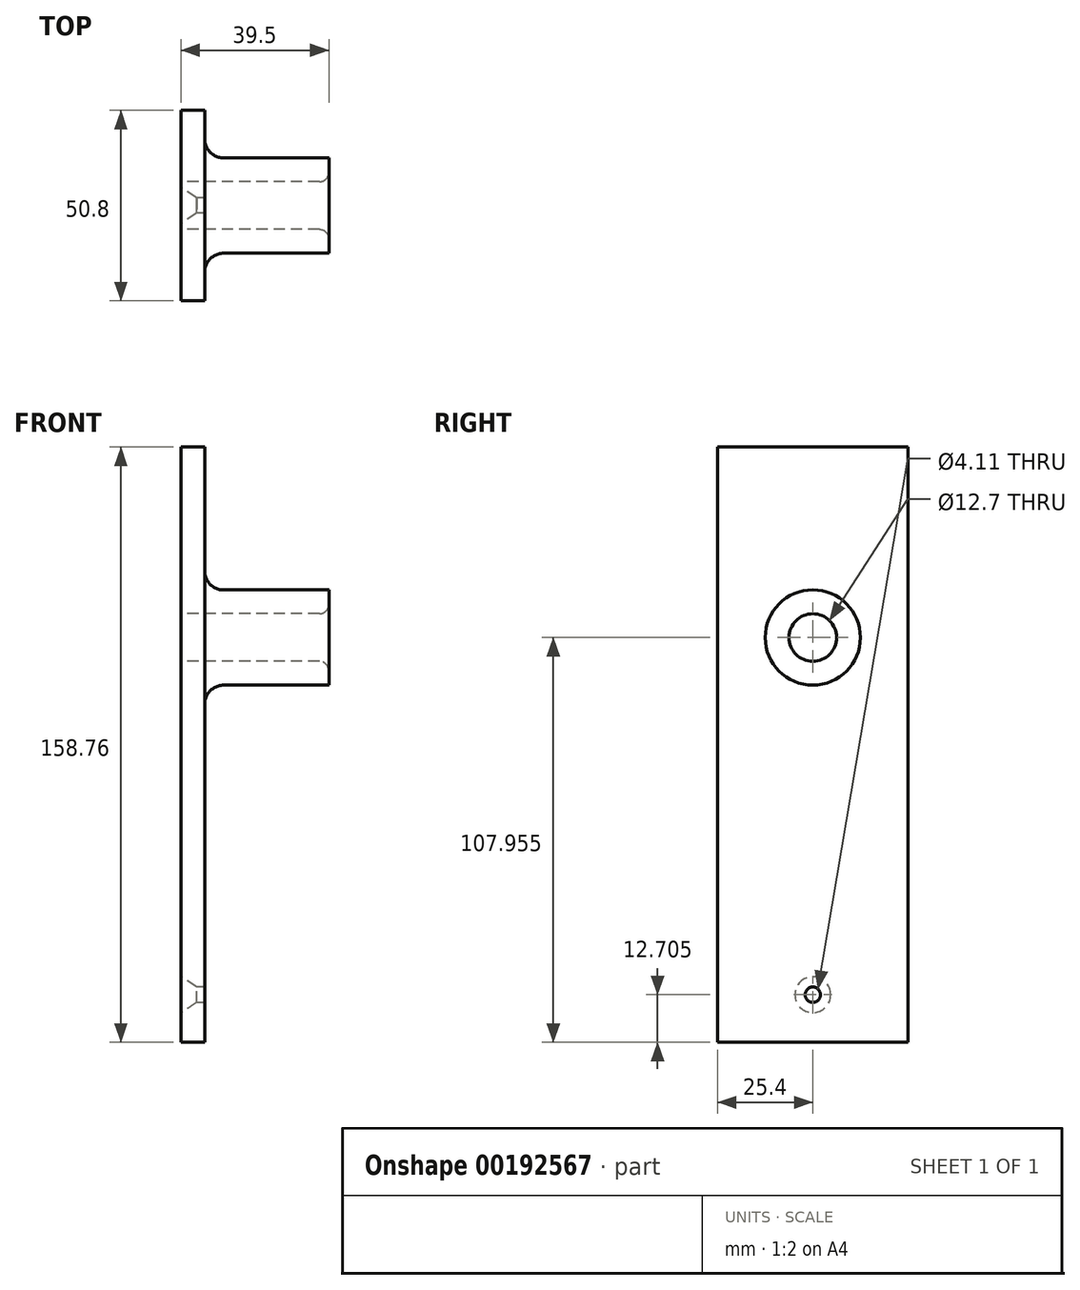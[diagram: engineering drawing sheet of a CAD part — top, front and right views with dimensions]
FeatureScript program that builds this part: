
annotation { "Feature Type Name" : "Feature", "Feature Type Description" : "" }
export const myFeature = defineFeature(function(context is Context, id is Id, definition is map)
    precondition{}
    {
        {
            var Q0;
            Q0=qCreatedBy(makeId("Right.planeOp"),FACE);
            var sketch = newSketch(context, id + "F0", { "sketchPlane" : qUnion([Q0])});
            skLineSegment(sketch, "E0.bottom", {"start": v(-25.4, 79.38) * mm, "end": v(25.4, 79.38) * mm});
            skLineSegment(sketch, "E0.top", {"start": v(-25.4, -79.37) * mm, "end": v(25.4, -79.37) * mm});
            skLineSegment(sketch, "E0.left", {"start": v(-25.4, 79.38) * mm, "end": v(-25.4, -79.37) * mm});
            skLineSegment(sketch, "E0.right", {"start": v(25.4, 79.38) * mm, "end": v(25.4, -79.37) * mm});
            skPoint(sketch, "E0.middle", {"position": v(0, 0) * mm});
            skLineSegment(sketch, "E1", {"start": v(0, 79.38) * mm, "end": v(0, 28.57) * mm});
            skPoint(sketch, "E1.endSnap0", {"position": v(0, 79.38) * mm});
            skLineSegment(sketch, "E2", {"start": v(0, 28.57) * mm, "end": v(0, -41.28) * mm});
            skLineSegment(sketch, "E3", {"start": v(0, -41.28) * mm, "end": v(0, -53.98) * mm});
            skLineSegment(sketch, "E4", {"start": v(0, -53.98) * mm, "end": v(0, -79.37) * mm});
            skCircle(sketch, "E5", {"center": v(0, 28.57) * mm, "radius": 12.7 * mm});
            skCircle(sketch, "E6", {"center": v(0, 28.57) * mm, "radius": 6.35 * mm});
            skCircle(sketch, "E7", {"center": v(0, -66.67) * mm, "radius": 2.06 * mm});
            skSolve(sketch);
        }
        {
            var Q0;
            {var subQ1=sQuery(id+"F0.wireOp",EDGE,"E0.left");Q0=makeQuery(id+"F0.imprint","IMPRINT",FACE,{"disambiguationData":[TD([[makeQuery(id+"F0.imprint","IMPRINT",EDGE,{"derivedFrom":subQ1}),1.0]])]});}
            var Q1;
            {var subQ1=sQuery(id+"F0.wireOp",EDGE,"E0.right");Q1=makeQuery(id+"F0.imprint","IMPRINT",FACE,{"disambiguationData":[TD([[makeQuery(id+"F0.imprint","IMPRINT",EDGE,{"derivedFrom":subQ1}),-1.0]])]});}
            var Q2;
            {var subQ0=sQuery(id+"F0.wireOp",EDGE,"E5");var subQ1=sQuery(id+"F0.wireOp",EDGE,"E1");var subQ2=makeQuery(id+"F0.imprint","INTERSECT",VERTEX,{"derivedFrom":[subQ1,subQ0]});Q2=makeQuery(id+"F0.imprint","IMPRINT",FACE,{"disambiguationData":[TD([[makeQuery(id+"F0.imprint","IMPRINT",EDGE,{"disambiguationData":[TD([[subQ2,-1.0]])],"derivedFrom":subQ1}),-1.0]])]});}
            var Q3;
            {var subQ0=sQuery(id+"F0.wireOp",EDGE,"E5");var subQ1=sQuery(id+"F0.wireOp",EDGE,"E1");var subQ2=makeQuery(id+"F0.imprint","INTERSECT",VERTEX,{"derivedFrom":[subQ1,subQ0]});Q3=makeQuery(id+"F0.imprint","IMPRINT",FACE,{"disambiguationData":[TD([[makeQuery(id+"F0.imprint","IMPRINT",EDGE,{"disambiguationData":[TD([[subQ2,-1.0]])],"derivedFrom":subQ1}),1.0]])]});}
            extrude(context, id + "F1", {"entities" : qUnion([Q0, Q1, Q2, Q3]), "depth" : 6.35 * mm});
        }
        {
            var Q0;
            {var subQ0=sQuery(id+"F0.wireOp",EDGE,"E5");var subQ1=sQuery(id+"F0.wireOp",EDGE,"E1");var subQ2=makeQuery(id+"F0.imprint","INTERSECT",VERTEX,{"derivedFrom":[subQ1,subQ0]});Q0=makeQuery(id+"F0.imprint","IMPRINT",FACE,{"disambiguationData":[TD([[makeQuery(id+"F0.imprint","IMPRINT",EDGE,{"disambiguationData":[TD([[subQ2,-1.0]])],"derivedFrom":subQ1}),-1.0]])]});}
            var Q1;
            {var subQ0=sQuery(id+"F0.wireOp",EDGE,"E5");var subQ1=sQuery(id+"F0.wireOp",EDGE,"E1");var subQ2=makeQuery(id+"F0.imprint","INTERSECT",VERTEX,{"derivedFrom":[subQ1,subQ0]});Q1=makeQuery(id+"F0.imprint","IMPRINT",FACE,{"disambiguationData":[TD([[makeQuery(id+"F0.imprint","IMPRINT",EDGE,{"disambiguationData":[TD([[subQ2,-1.0]])],"derivedFrom":subQ1}),1.0]])]});}
            extrude(context, id + "F2", {"entities" : qUnion([Q0, Q1]), "operationType" : NewBodyOperationType.ADD, "depth" : 39.5 * mm});
        }
        {
            var Q0;
            Q0=makeQuery(id+"F1.opExtrude","CAP_EDGE",EDGE,{"disambiguationData":[OSD([sQuery(id+"F0.wireOp",EDGE,"E7")])],"isStart":true});
            chamfer(context, id + "F3", {"entities" : qUnion([Q0]), "chamferType" : ChamferType.TWO_OFFSETS, "width1" : 2.72 * mm, "oppositeDirection" : false, "width2" : 4.27 * mm, "tangentPropagation" : true});
        }
        {
            var Q0;
            Q0=makeQuery(id+"F2.boolean.opBoolean","INTERSECT",EDGE,{"derivedFrom":[makeQuery(id+"F1.opExtrude","CAP_FACE",FACE,{"disambiguationData":[OSD([sQuery(id+"F0.wireOp",EDGE,"E0.bottom"),sQuery(id+"F0.wireOp",EDGE,"E0.top"),sQuery(id+"F0.wireOp",EDGE,"E0.left"),sQuery(id+"F0.wireOp",EDGE,"E0.right"),sQuery(id+"F0.wireOp",EDGE,"E6"),sQuery(id+"F0.wireOp",EDGE,"E7")])],"isStart":false}),makeQuery(id+"F2.opExtrude","SWEPT_FACE",FACE,{"disambiguationData":[OSD([sQuery(id+"F0.wireOp",EDGE,"E5")])]})]});
            fillet(context, id + "F4", {"entities" : qUnion([Q0]), "radius" : 5.08 * mm, "tangentPropagation" : true, "allowEdgeOverflow" : false});
        }
        {
            var Q0;
            Q0=makeQuery(id+"F2.opExtrude","CAP_EDGE",EDGE,{"disambiguationData":[OSD([sQuery(id+"F0.wireOp",EDGE,"E6")])],"isStart":false});
            fillet(context, id + "F5", {"entities" : qUnion([Q0]), "radius" : 2.54 * mm, "tangentPropagation" : true, "allowEdgeOverflow" : false});
        }
    });
